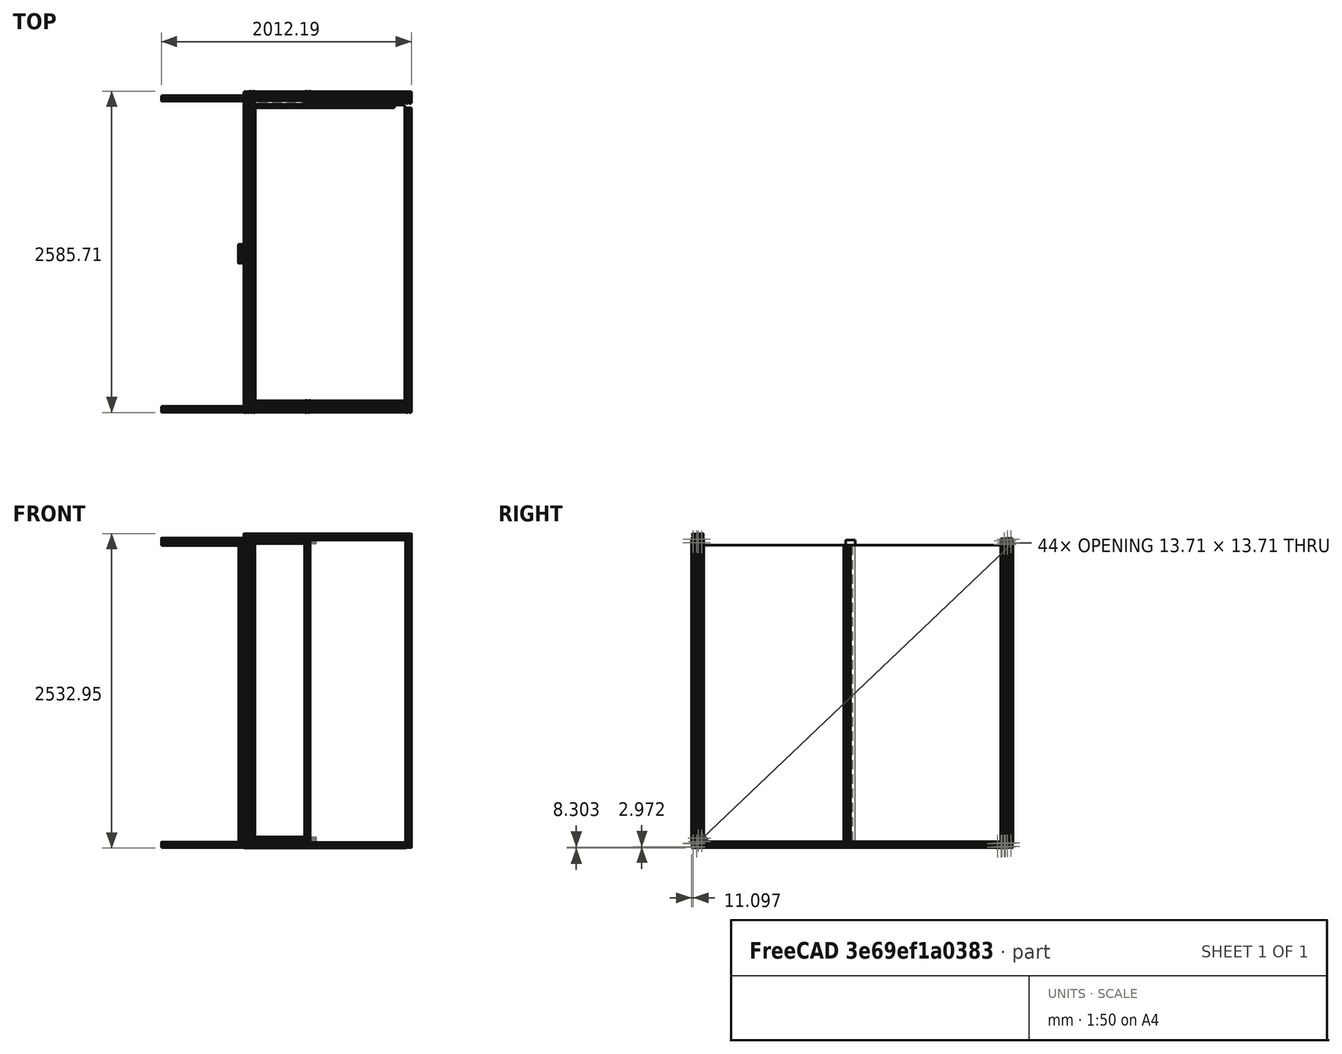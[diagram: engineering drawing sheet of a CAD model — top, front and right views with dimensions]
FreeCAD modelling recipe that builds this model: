
FCSTD DOCUMENT  (FreeCAD 0.20R)
Label: arena
License: All rights reserved
LicenseURL: http://en.wikipedia.org/wiki/All_rights_reserved
objects: PartDesign::Pad×36, PartDesign::Body×36, PartDesign::FeatureBase×28, Sketcher::SketchObject×9, Part::FeaturePython×8, App::DocumentObjectGroup×7, Part::Feature×6, TechDraw::DrawViewPart×3, TechDraw::DrawSVGTemplate×2, TechDraw::DrawPage×2, Spreadsheet::Sheet×1
note: 159 computed .brp shape members not serialized (recipe doc carries the construction recipe); baked Part::Feature solids carry a one-line shape summary decoded from their .brp

FEATURE [Part::Feature] Part__Feature  label="5537T041_T-Slotted Framing"
  shape: bbox 90 x 45 x 152.4 mm, 277 faces (baked)
FEATURE [Part::FeaturePython] Facebinder  label="double"  # WARN: FeaturePython — macro-defined, semantics opaque (R4)
  Area = 1339.39
  Extrusion = 0
  Faces = -> [Part__Feature]
  RemoveSplitter = false
  Sew = false
FEATURE [PartDesign::FeatureBase] BaseFeature
  BaseFeature = -> Facebinder
FEATURE [PartDesign::Pad] Pad
  BaseFeature = -> BaseFeature
  Direction = (0,0,1)
  Length = 2438.4
  Length2 = 10
  Profile = -> BaseFeature
  Type = 0
FEATURE [PartDesign::Body] Body  label="bottom"
  BaseFeature = -> Facebinder
  Group = -> [BaseFeature,Pad]
  Origin = -> Origin
  Placement = pos=(95.0976,0,46.5582) rot=(0,0,1;0rad)
  Tip = -> Pad
FEATURE [PartDesign::FeatureBase] BaseFeature001
  BaseFeature = -> Facebinder
FEATURE [PartDesign::Pad] Pad001
  BaseFeature = -> BaseFeature001
  Direction = (0,0,1)
  Length = 1348.13
  Length2 = 10
  Profile = -> BaseFeature001
  Type = 0
FEATURE [PartDesign::Body] Body001  label="wall"
  BaseFeature = -> Facebinder
  Group = -> [BaseFeature001,Pad001]
  Origin = -> Origin001
  Placement = pos=(-25.4,27.7368,101.6) rot=(0.57735,-0.57735,0.57735;4.18879rad)
  Tip = -> Pad001
FEATURE [Part::Feature] Part__Feature001  label="single-extrusion"
  shape: bbox 45 x 45 x 152.4 mm, 246 faces (baked)
FEATURE [Part::FeaturePython] Facebinder001  label="single001-face"  # WARN: FeaturePython — macro-defined, semantics opaque (R4)
  Area = 538.918
  Extrusion = 0
  Faces = -> [Part__Feature001]
  RemoveSplitter = false
  Sew = false
FEATURE [PartDesign::FeatureBase] BaseFeature002
  BaseFeature = -> Facebinder001
FEATURE [PartDesign::Pad] Pad002
  BaseFeature = -> BaseFeature002
  Direction = (0,0,1)
  Length = 2438.4
  Length2 = 10
  Profile = -> BaseFeature002
  Type = 0
FEATURE [PartDesign::Body] Body002  label="top001"
  BaseFeature = -> Facebinder001
  Group = -> [BaseFeature002,Pad002]
  Origin = -> Origin002
  Placement = pos=(1375.94,0,48.5394) rot=(0,0,1;0rad)
  Tip = -> Pad002
FEATURE [PartDesign::FeatureBase] BaseFeature003
  BaseFeature = -> Facebinder001
FEATURE [PartDesign::Pad] Pad003
  BaseFeature = -> BaseFeature003
  Direction = (0,0,1)
  Length = 2438.4
  Length2 = 10
  Profile = -> BaseFeature003
  Type = 0
FEATURE [PartDesign::Body] Body003  label="center"
  BaseFeature = -> Facebinder001
  Group = -> [BaseFeature003,Pad003]
  Origin = -> Origin003
  Placement = pos=(561.213,0,50.8) rot=(0,0,1;0rad)
  Tip = -> Pad003
FEATURE [PartDesign::FeatureBase] BaseFeature004
  BaseFeature = -> Facebinder001
FEATURE [PartDesign::Pad] Pad004
  BaseFeature = -> BaseFeature004
  Direction = (0,0,1)
  Length = 2438.4
  Length2 = 10
  Profile = -> BaseFeature004
  Type = 0
FEATURE [PartDesign::Body] Body004  label="bottom-window"
  BaseFeature = -> Facebinder001
  Group = -> [BaseFeature004,Pad004]
  Origin = -> Origin004
  Placement = pos=(114.3,51.511,48.539) rot=(0,0,1;0rad)
  Tip = -> Pad004
FEATURE [Part::Feature] Part__Feature002  label="single003"
  shape: bbox 45 x 45 x 152.4 mm, 246 faces (baked)
FEATURE [Part::FeaturePython] Facebinder002  label="single002"  # WARN: FeaturePython — macro-defined, semantics opaque (R4)
  Area = 538.918
  Extrusion = 0
  Faces = -> [Part__Feature002]
  RemoveSplitter = false
  Sew = false
FEATURE [PartDesign::FeatureBase] BaseFeature005
  BaseFeature = -> Facebinder002
FEATURE [PartDesign::Pad] Pad005
  BaseFeature = -> BaseFeature005
  Direction = (0,0,1)
  Length = 2438.4
  Length2 = 10
  Profile = -> BaseFeature005
  Type = 0
FEATURE [PartDesign::Body] Body005  label="top-window001"
  BaseFeature = -> Facebinder002
  Group = -> [BaseFeature005,Pad005]
  Origin = -> Origin005
  Placement = pos=(564.185,51.511,48.539) rot=(0,0,1;0rad)
  Tip = -> Pad005
FEATURE [PartDesign::FeatureBase] BaseFeature006
  BaseFeature = -> Facebinder002
FEATURE [PartDesign::Pad] Pad006
  BaseFeature = -> BaseFeature006
  Direction = (0,0,1)
  Length = 490.322
  Length2 = 10
  Profile = -> BaseFeature006
  Type = 0
  expr: Length = <<Spreadsheet>>.window_height
FEATURE [PartDesign::Body] Body006  label="window-wall"
  BaseFeature = -> Facebinder002
  Group = -> [BaseFeature006,Pad006]
  Origin = -> Origin006
  Placement = pos=(14.859,45.5676,103.022) rot=(0,1,0;1.5708rad)
  Tip = -> Pad006
FEATURE [Sketcher::SketchObject] Sketch
  FullyConstrained = false
  MapMode = 5
  Placement = pos=(0,0,0) rot=(1,0,0;1.5708rad)
  Support = -> [XZ_Plane008]
  sketch-geometry (4):
    g0: LineSegment StartX=932.741 StartY=2717.77 StartZ=0 EndX=1745.54 EndY=2717.77 EndZ=0
    g1: LineSegment StartX=1745.54 StartY=2717.77 StartZ=0 EndX=1745.54 EndY=279.367 EndZ=0
    g2: LineSegment StartX=1745.54 StartY=279.367 StartZ=0 EndX=932.741 EndY=279.367 EndZ=0
    g3: LineSegment StartX=932.741 StartY=279.367 StartZ=0 EndX=932.741 EndY=2717.77 EndZ=0
  constraints (10):
    c: Coincident(g0,g1)
    c: Coincident(g1,g2)
    c: Coincident(g2,g3)
    c: Coincident(g3,g0)
    c: Horizontal(g0)
    c: Horizontal(g2)
    c: Vertical(g1)
    c: Vertical(g3)
    c: DistanceY(g1,g1) = 2438.4
    c: DistanceX(g0,g0) = 812.8
FEATURE [PartDesign::Pad] Pad008
  Direction = (0,-1,2e-16)
  Length = 9.525
  Length2 = 10
  Placement = pos=(0,0,0) rot=(1,0,0;1.5708rad)
  Profile = -> Sketch
  ReferenceAxis = -> Sketch [N_Axis]
  Type = 0
FEATURE [PartDesign::Body] Body008  label="upper polycarb"
  Group = -> [Sketch,Pad008]
  Origin = -> Origin008
  Placement = pos=(-383.362,0,-162.458) rot=(0,0,1;0rad)
  Tip = -> Pad008
FEATURE [Sketcher::SketchObject] Sketch001
  FullyConstrained = false
  MapMode = 5
  Placement = pos=(0,0,0) rot=(1,0,0;1.5708rad)
  Support = -> [XZ_Plane008]
  sketch-geometry (4):
    g0: LineSegment StartX=527.842 StartY=2715.74 StartZ=0 EndX=934.242 EndY=2715.74 EndZ=0
    g1: LineSegment StartX=934.242 StartY=2715.74 StartZ=0 EndX=934.242 EndY=277.345 EndZ=0
    g2: LineSegment StartX=934.242 StartY=277.345 StartZ=0 EndX=527.842 EndY=277.345 EndZ=0
    g3: LineSegment StartX=527.842 StartY=277.345 StartZ=0 EndX=527.842 EndY=2715.74 EndZ=0
  constraints (10):
    c: Coincident(g0,g1)
    c: Coincident(g1,g2)
    c: Coincident(g2,g3)
    c: Coincident(g3,g0)
    c: Horizontal(g0)
    c: Horizontal(g2)
    c: Vertical(g1)
    c: Vertical(g3)
    c: DistanceY(g1,g1) = 2438.4
    c: DistanceX(g0,g0) = 406.4
FEATURE [PartDesign::Pad] Pad009
  Direction = (0,-1,2e-16)
  Length = 9.525
  Length2 = 10
  Placement = pos=(0,0,0) rot=(1,0,0;1.5708rad)
  Profile = -> Sketch001
  ReferenceAxis = -> Sketch001 [N_Axis]
  Type = 0
FEATURE [PartDesign::Body] Body009  label="lower polycarb"
  Group = -> [Sketch001,Pad009]
  Origin = -> Origin009
  Placement = pos=(-389.306,54.483,-162.458) rot=(0,0,1;0rad)
  Tip = -> Pad009
FEATURE [Part::FeaturePython] Facebinder003  label="double001"  # WARN: FeaturePython — macro-defined, semantics opaque (R4)
  Area = 1339.39
  Extrusion = 0
  Faces = -> [Part__Feature]
  RemoveSplitter = false
  Sew = false
FEATURE [PartDesign::FeatureBase] BaseFeature008
  BaseFeature = -> Facebinder003
FEATURE [PartDesign::Pad] Pad010
  BaseFeature = -> BaseFeature008
  Direction = (0,0,1)
  Length = 2438.4
  Length2 = 10
  Profile = -> BaseFeature008
  Type = 0
FEATURE [PartDesign::Body] Body010  label="bottom001"
  BaseFeature = -> Facebinder003
  Group = -> [BaseFeature008,Pad010]
  Origin = -> Origin010
  Placement = pos=(96.0882,40.6146,103.022) rot=(1,0,0;1.5708rad)
  Tip = -> Pad010
FEATURE [Part::FeaturePython] Facebinder004  label="single001-face001"  # WARN: FeaturePython — macro-defined, semantics opaque (R4)
  Area = 538.918
  Extrusion = 0
  Faces = -> [Part__Feature001]
  RemoveSplitter = false
  Sew = false
FEATURE [PartDesign::FeatureBase] BaseFeature009
  BaseFeature = -> Facebinder004
FEATURE [PartDesign::Pad] Pad011
  BaseFeature = -> BaseFeature009
  Direction = (0,0,1)
  Length = 2387.6
  Length2 = 10
  Profile = -> BaseFeature009
  Type = 0
  expr: Length = <<Spreadsheet>>.horizontal_length
FEATURE [PartDesign::Body] Body011  label="top"
  BaseFeature = -> Facebinder004
  Group = -> [BaseFeature009,Pad011]
  Origin = -> Origin011
  Placement = pos=(1375.94,17.8308,101.041) rot=(1,0,0;1.5708rad)
  Tip = -> Pad011
FEATURE [PartDesign::FeatureBase] BaseFeature010
  BaseFeature = -> Facebinder004
FEATURE [PartDesign::Pad] Pad012
  BaseFeature = -> BaseFeature010
  Direction = (0,0,1)
  Length = 1213.36
  Length2 = 10
  Profile = -> BaseFeature010
  Type = 0
  expr: Length = <<Spreadsheet>>.side_length
FEATURE [PartDesign::Body] Body012  label="side"
  BaseFeature = -> Facebinder004
  Group = -> [BaseFeature010,Pad012]
  Origin = -> Origin012
  Placement = pos=(-25.7556,-35.6616,98.0694) rot=(0,1,0;1.5708rad)
  Tip = -> Pad012
FEATURE [Sketcher::SketchObject] Sketch002
  FullyConstrained = false
  MapMode = 5
  Support = -> [XY_Plane013]
  sketch-geometry (4):
    g0: LineSegment StartX=127.47 StartY=-36.9995 StartZ=0 EndX=1346.67 EndY=-36.9995 EndZ=0
    g1: LineSegment StartX=1346.67 StartY=-36.9995 StartZ=0 EndX=1346.67 EndY=-2475.4 EndZ=0
    g2: LineSegment StartX=1346.67 StartY=-2475.4 StartZ=0 EndX=127.47 EndY=-2475.4 EndZ=0
    g3: LineSegment StartX=127.47 StartY=-2475.4 StartZ=0 EndX=127.47 EndY=-36.9995 EndZ=0
  constraints (10):
    c: Coincident(g0,g1)
    c: Coincident(g1,g2)
    c: Coincident(g2,g3)
    c: Coincident(g3,g0)
    c: Horizontal(g0)
    c: Horizontal(g2)
    c: Vertical(g1)
    c: Vertical(g3)
    c: DistanceX(g0,g0) = 1219.2
    c: DistanceY(g1,g1) = 2438.4
FEATURE [PartDesign::Pad] Pad013
  Direction = (0,0,1)
  Length = 9.525
  Length2 = 10
  Profile = -> Sketch002
  ReferenceAxis = -> Sketch002 [N_Axis]
  Type = 0
FEATURE [PartDesign::Body] Body013  label="side-polycarb"
  Group = -> [Sketch002,Pad013]
  Origin = -> Origin013
  Placement = pos=(0,0,93.1164) rot=(0,0,1;0rad)
  Tip = -> Pad013
FEATURE [PartDesign::FeatureBase] BaseFeature011
  BaseFeature = -> Facebinder004
FEATURE [PartDesign::Pad] Pad014
  BaseFeature = -> BaseFeature011
  Direction = (0,0,1)
  Length = 1303.02
  Length2 = 10
  Profile = -> BaseFeature011
  Type = 0
FEATURE [PartDesign::Body] Body014  label="side001"
  BaseFeature = -> Facebinder004
  Group = -> [BaseFeature011,Pad014]
  Origin = -> Origin014
  Placement = pos=(-25.7556,-2486.41,98.0694) rot=(0,1,0;1.5708rad)
  Tip = -> Pad014
FEATURE [App::DocumentObjectGroup] Group001  label="static-side"
  Group = -> [Facebinder003,Body010,Body011,Body012,Body013,Body014]
FEATURE [Spreadsheet::Sheet] Spreadsheet
  cells = C1=length; D1=length (mm); E1=quantity; F1=price per; G1=price; A2=static-sides; A3=bottom; B3=4590x96; C3=94; D3(horizontal_length)==C3 * 25.4; E3=2; F3=140; G3==E3 * F3; A4=top; B4=4545x96; C4=94; D4==C4 * 25.4; E4=2; F4=44; G4==E4 * F4; A5=sides; B5=4545x48; C5=47.77; D5(side_length)==C5 * 25.4; E5=4; F5=23; G5==E5 * F5; A6=polycarb; C6==C5 + 2 * 0.5; A8=window-sides; A9=bottom; B9=4590x96; C9=94; D9==C9 * 25.4; E9=2; F9=140; G9==E9 * F9; A10=top; B10=4545x96; C10=94; D10==C10 * 25.4; E10=2; F10=44; G10==E10 * F10; A11=sides; B11=4545x48; C11=53.08; D11==C11 * 25.4; E11=4; F11=23; G11==E11 * F11; A12=top/bot; B12=4545x96; C12=94; D12==C12 * 25.4; E12=4; F12=44; G12==E12 * F12; A13=sides; B13=4545x18; C13==15.76 + 2 * 1.772; D13(window_height)==C13 * 25.4; E13=4; F13=10; G13==E13 * F13; A15=roof; A16=crossbar; B16=4545x96; C16=94; D16==C16 * 25.4; E16=1; F16=44; G16==E16 * F16; A17=feet; B17=4545x32; C17=26; D17(foot_length)==C17 * 25.4; E17=5; A18=floor-brace; B18=4545; C18==C3; A19=floor-brace-support; B19=4545; C19=6; F19=total; G19==sum(G3:G16)
FEATURE [PartDesign::FeatureBase] BaseFeature012
  BaseFeature = -> Facebinder002
FEATURE [PartDesign::Pad] Pad015
  BaseFeature = -> BaseFeature012
  Direction = (0,0,1)
  Length = 490.322
  Length2 = 10
  Profile = -> BaseFeature012
  Type = 0
  expr: Length = <<Spreadsheet>>.window_height
FEATURE [PartDesign::Body] Body015  label="window-wall001"
  BaseFeature = -> Facebinder002
  Group = -> [BaseFeature012,Pad015]
  Origin = -> Origin015
  Placement = pos=(64.389,45.5676,2548.81) rot=(0,1,0;1.5708rad)
  Tip = -> Pad015
FEATURE [PartDesign::FeatureBase] BaseFeature013
  BaseFeature = -> Facebinder004
FEATURE [PartDesign::Pad] Pad016
  BaseFeature = -> BaseFeature013
  Direction = (0,0,1)
  Length = 2387.6
  Length2 = 10
  Profile = -> BaseFeature013
  Type = 0
  expr: Length = <<Spreadsheet>>.horizontal_length
FEATURE [PartDesign::Body] Body016  label="crossbar"
  BaseFeature = -> Facebinder004
  Group = -> [BaseFeature013,Pad016]
  Origin = -> Origin016
  Placement = pos=(1375.94,-1264.01,44.577) rot=(0,0,1;0rad)
  Tip = -> Pad016
FEATURE [App::DocumentObjectGroup] Group002  label="roof"
  Group = -> [Body016]
FEATURE [PartDesign::FeatureBase] BaseFeature014
  BaseFeature = -> Facebinder004
FEATURE [PartDesign::Pad] Pad017
  BaseFeature = -> BaseFeature014
  Direction = (0,0,1)
  Length = 660.4
  Length2 = 10
  Profile = -> BaseFeature014
  Type = 0
  expr: Length = <<Spreadsheet>>.foot_length
FEATURE [PartDesign::Body] Body017  label="foot"
  BaseFeature = -> Facebinder004
  Group = -> [BaseFeature014,Pad017]
  Origin = -> Origin017
  Placement = pos=(-689.458,17.8308,101.041) rot=(0.57735,0.57735,0.57735;2.0944rad)
  Tip = -> Pad017
FEATURE [Sketcher::SketchObject] Sketch003  label="people"
  FullyConstrained = false
  MapMode = 5
  Placement = pos=(0,0,0) rot=(1,0,0;1.5708rad)
  Support = -> [XZ_Plane013]
  sketch-geometry (8):
    g0: LineSegment StartX=-565.128 StartY=2175.86 StartZ=0 EndX=1212.87 EndY=2175.86 EndZ=0
    g1: LineSegment StartX=1212.87 StartY=2175.86 StartZ=0 EndX=1212.87 EndY=1762.45 EndZ=0
    g2: LineSegment StartX=1212.87 StartY=1762.45 StartZ=0 EndX=-565.128 EndY=1762.45 EndZ=0
    g3: LineSegment StartX=-565.128 StartY=1762.45 StartZ=0 EndX=-565.128 EndY=2175.86 EndZ=0
    g4: LineSegment StartX=-565.128 StartY=669.762 StartZ=0 EndX=654.072 EndY=669.762 EndZ=0
    g5: LineSegment StartX=654.072 StartY=669.762 StartZ=0 EndX=654.072 EndY=256.353 EndZ=0
    g6: LineSegment StartX=654.072 StartY=256.353 StartZ=0 EndX=-565.128 EndY=256.353 EndZ=0
    g7: LineSegment StartX=-565.128 StartY=256.353 StartZ=0 EndX=-565.128 EndY=669.762 EndZ=0
  constraints (20):
    c: Coincident(g0,g1)
    c: Coincident(g1,g2)
    c: Coincident(g2,g3)
    c: Coincident(g3,g0)
    c: Horizontal(g0)
    c: Horizontal(g2)
    c: Vertical(g1)
    c: Vertical(g3)
    c: Coincident(g4,g5)
    c: Coincident(g5,g6)
    c: Coincident(g6,g7)
    c: Coincident(g7,g4)
    c: Horizontal(g4)
    c: Horizontal(g6)
    c: Vertical(g5)
    c: Vertical(g7)
    c: DistanceX(g0,g0) = 1778
    c: DistanceX(g4,g4) = 1219.2
    c: Vertical(g2,g4)
    c: Equal(g3,g7)
FEATURE [PartDesign::FeatureBase] BaseFeature015
  BaseFeature = -> Facebinder004
FEATURE [PartDesign::Pad] Pad018
  BaseFeature = -> BaseFeature015
  Direction = (0,0,1)
  Length = 660.4
  Length2 = 10
  Profile = -> BaseFeature015
  Type = 0
  expr: Length = <<Spreadsheet>>.foot_length
FEATURE [PartDesign::Body] Body018  label="foot001"
  BaseFeature = -> Facebinder004
  Group = -> [BaseFeature015,Pad018]
  Origin = -> Origin018
  Placement = pos=(-689.458,17.8308,2535.94) rot=(0.57735,0.57735,0.57735;2.0944rad)
  Tip = -> Pad018
FEATURE [PartDesign::FeatureBase] BaseFeature016
  BaseFeature = -> Facebinder004
FEATURE [PartDesign::Pad] Pad019
  BaseFeature = -> BaseFeature016
  Direction = (0,0,1)
  Length = 660.4
  Length2 = 10
  Profile = -> BaseFeature016
  Type = 0
  expr: Length = <<Spreadsheet>>.foot_length
FEATURE [PartDesign::Body] Body019  label="foot002"
  BaseFeature = -> Facebinder004
  Group = -> [BaseFeature016,Pad019]
  Origin = -> Origin019
  Placement = pos=(-689.458,-2486.41,101.041) rot=(0.57735,0.57735,0.57735;2.0944rad)
  Tip = -> Pad019
FEATURE [PartDesign::FeatureBase] BaseFeature017
  BaseFeature = -> Facebinder004
FEATURE [PartDesign::Pad] Pad020
  BaseFeature = -> BaseFeature017
  Direction = (0,0,1)
  Length = 660.4
  Length2 = 10
  Profile = -> BaseFeature017
  Type = 0
  expr: Length = <<Spreadsheet>>.foot_length
FEATURE [PartDesign::Body] Body020  label="foot003"
  BaseFeature = -> Facebinder004
  Group = -> [BaseFeature017,Pad020]
  Origin = -> Origin020
  Placement = pos=(-689.458,-2485.42,2549.8) rot=(0.57735,0.57735,0.57735;2.0944rad)
  Tip = -> Pad020
FEATURE [App::DocumentObjectGroup] Group003  label="feet"
  Group = -> [Body017,Body018,Body019,Body020]
FEATURE [Part::Feature] Part__Feature003  label="5537T041_T-Slotted Framing001"
  shape: bbox 90 x 45 x 152.4 mm, 277 faces (baked)
FEATURE [Part::FeaturePython] Facebinder005  label="double002"  # WARN: FeaturePython — macro-defined, semantics opaque (R4)
  Area = 1339.39
  Extrusion = 0
  Faces = -> [Part__Feature003]
  RemoveSplitter = false
  Sew = false
FEATURE [PartDesign::FeatureBase] BaseFeature018
  BaseFeature = -> Facebinder005
FEATURE [PartDesign::FeatureBase] BaseFeature019
  BaseFeature = -> Facebinder005
FEATURE [PartDesign::Pad] Pad021
  BaseFeature = -> BaseFeature018
  Direction = (0,0,1)
  Length = 2438.4
  Length2 = 10
  Profile = -> BaseFeature018
  Type = 0
FEATURE [PartDesign::Body] Body021  label="bottom002"
  BaseFeature = -> Facebinder005
  Group = -> [BaseFeature018,Pad021]
  Origin = -> Origin021
  Placement = pos=(95.098,-2489.2,46.558) rot=(0,0,1;0rad)
  Tip = -> Pad021
FEATURE [PartDesign::Pad] Pad022
  BaseFeature = -> BaseFeature019
  Direction = (0,0,1)
  Length = 1348.13
  Length2 = 10
  Profile = -> BaseFeature019
  Type = 0
FEATURE [PartDesign::Body] Body022  label="wall001"
  BaseFeature = -> Facebinder005
  Group = -> [BaseFeature019,Pad022]
  Origin = -> Origin022
  Placement = pos=(-25.4,-2461.46,2586.02) rot=(0.57735,-0.57735,0.57735;4.18879rad)
  Tip = -> Pad022
FEATURE [Part::Feature] Part__Feature004  label="single-extrusion001"
  shape: bbox 45 x 45 x 152.4 mm, 246 faces (baked)
FEATURE [Part::FeaturePython] Facebinder006  label="single001-face002"  # WARN: FeaturePython — macro-defined, semantics opaque (R4)
  Area = 538.918
  Extrusion = 0
  Faces = -> [Part__Feature004]
  RemoveSplitter = false
  Sew = false
FEATURE [PartDesign::FeatureBase] BaseFeature020
  BaseFeature = -> Facebinder006
FEATURE [PartDesign::FeatureBase] BaseFeature021
  BaseFeature = -> Facebinder006
FEATURE [PartDesign::FeatureBase] BaseFeature022
  BaseFeature = -> Facebinder006
FEATURE [PartDesign::Pad] Pad023
  BaseFeature = -> BaseFeature020
  Direction = (0,0,1)
  Length = 2438.4
  Length2 = 10
  Profile = -> BaseFeature020
  Type = 0
FEATURE [PartDesign::Body] Body023  label="top002"
  BaseFeature = -> Facebinder006
  Group = -> [BaseFeature020,Pad023]
  Origin = -> Origin023
  Placement = pos=(1375.94,-2489.2,48.539) rot=(0,0,1;0rad)
  Tip = -> Pad023
FEATURE [PartDesign::Pad] Pad024
  BaseFeature = -> BaseFeature021
  Direction = (0,0,1)
  Length = 2438.4
  Length2 = 10
  Profile = -> BaseFeature021
  Type = 0
FEATURE [PartDesign::Body] Body024  label="center001"
  BaseFeature = -> Facebinder006
  Group = -> [BaseFeature021,Pad024]
  Origin = -> Origin024
  Placement = pos=(561.213,-2489.2,50.8) rot=(0,0,1;0rad)
  Tip = -> Pad024
FEATURE [PartDesign::Pad] Pad025
  BaseFeature = -> BaseFeature022
  Direction = (0,0,1)
  Length = 2438.4
  Length2 = 10
  Profile = -> BaseFeature022
  Type = 0
FEATURE [PartDesign::Body] Body025  label="bottom-window001"
  BaseFeature = -> Facebinder006
  Group = -> [BaseFeature022,Pad025]
  Origin = -> Origin025
  Placement = pos=(114.3,-2437.69,48.539) rot=(0,0,1;0rad)
  Tip = -> Pad025
FEATURE [Part::Feature] Part__Feature005  label="single005"
  shape: bbox 45 x 45 x 152.4 mm, 246 faces (baked)
FEATURE [Part::FeaturePython] Facebinder007  label="single004"  # WARN: FeaturePython — macro-defined, semantics opaque (R4)
  Area = 538.918
  Extrusion = 0
  Faces = -> [Part__Feature005]
  RemoveSplitter = false
  Sew = false
FEATURE [PartDesign::FeatureBase] BaseFeature023
  BaseFeature = -> Facebinder007
FEATURE [PartDesign::FeatureBase] BaseFeature024
  BaseFeature = -> Facebinder007
FEATURE [PartDesign::FeatureBase] BaseFeature025
  BaseFeature = -> Facebinder007
FEATURE [PartDesign::Pad] Pad026
  BaseFeature = -> BaseFeature023
  Direction = (0,0,1)
  Length = 2438.4
  Length2 = 10
  Profile = -> BaseFeature023
  Type = 0
FEATURE [PartDesign::Body] Body026  label="top-window002"
  BaseFeature = -> Facebinder007
  Group = -> [BaseFeature023,Pad026]
  Origin = -> Origin026
  Placement = pos=(564.185,-2437.69,48.539) rot=(0,0,1;0rad)
  Tip = -> Pad026
FEATURE [PartDesign::Pad] Pad027
  BaseFeature = -> BaseFeature024
  Direction = (0,0,1)
  Length = 490.322
  Length2 = 10
  Profile = -> BaseFeature024
  Type = 0
  expr: Length = <<Spreadsheet>>.window_height
FEATURE [PartDesign::Body] Body027  label="window-wall002"
  BaseFeature = -> Facebinder007
  Group = -> [BaseFeature024,Pad027]
  Origin = -> Origin027
  Placement = pos=(64.389,-2443.63,142.646) rot=(0,1,0;1.5708rad)
  Tip = -> Pad027
FEATURE [PartDesign::Pad] Pad030
  BaseFeature = -> BaseFeature025
  Direction = (0,0,1)
  Length = 490.322
  Length2 = 10
  Profile = -> BaseFeature025
  Type = 0
  expr: Length = <<Spreadsheet>>.window_height
FEATURE [PartDesign::Body] Body030  label="window-wall003"
  BaseFeature = -> Facebinder007
  Group = -> [BaseFeature025,Pad030]
  Origin = -> Origin030
  Placement = pos=(64.389,-2443.63,2548.81) rot=(0,1,0;1.5708rad)
  Tip = -> Pad030
FEATURE [Sketcher::SketchObject] Sketch004
  FullyConstrained = false
  MapMode = 5
  Placement = pos=(0,0,0) rot=(1,0,0;1.5708rad)
  Support = -> [XZ_Plane028]
  sketch-geometry (4):
    g0: LineSegment StartX=932.741 StartY=2717.77 StartZ=0 EndX=1745.54 EndY=2717.77 EndZ=0
    g1: LineSegment StartX=1745.54 StartY=2717.77 StartZ=0 EndX=1745.54 EndY=279.367 EndZ=0
    g2: LineSegment StartX=1745.54 StartY=279.367 StartZ=0 EndX=932.741 EndY=279.367 EndZ=0
    g3: LineSegment StartX=932.741 StartY=279.367 StartZ=0 EndX=932.741 EndY=2717.77 EndZ=0
  constraints (10):
    c: Coincident(g0,g1)
    c: Coincident(g1,g2)
    c: Coincident(g2,g3)
    c: Coincident(g3,g0)
    c: Horizontal(g0)
    c: Horizontal(g2)
    c: Vertical(g1)
    c: Vertical(g3)
    c: DistanceY(g1,g1) = 2438.4
    c: DistanceX(g0,g0) = 812.8
FEATURE [PartDesign::Pad] Pad028
  Direction = (0,-1,2e-16)
  Length = 9.525
  Length2 = 10
  Placement = pos=(0,0,0) rot=(1,0,0;1.5708rad)
  Profile = -> Sketch004
  ReferenceAxis = -> Sketch004 [N_Axis]
  Type = 0
FEATURE [PartDesign::Body] Body028  label="upper polycarb001"
  Group = -> [Sketch004,Pad028]
  Origin = -> Origin028
  Placement = pos=(-383.362,-2489.2,-162.458) rot=(0,0,1;0rad)
  Tip = -> Pad028
FEATURE [Sketcher::SketchObject] Sketch005
  FullyConstrained = false
  MapMode = 5
  Placement = pos=(0,0,0) rot=(1,0,0;1.5708rad)
  Support = -> [XZ_Plane028]
  sketch-geometry (4):
    g0: LineSegment StartX=527.842 StartY=2715.74 StartZ=0 EndX=934.242 EndY=2715.74 EndZ=0
    g1: LineSegment StartX=934.242 StartY=2715.74 StartZ=0 EndX=934.242 EndY=277.345 EndZ=0
    g2: LineSegment StartX=934.242 StartY=277.345 StartZ=0 EndX=527.842 EndY=277.345 EndZ=0
    g3: LineSegment StartX=527.842 StartY=277.345 StartZ=0 EndX=527.842 EndY=2715.74 EndZ=0
  constraints (10):
    c: Coincident(g0,g1)
    c: Coincident(g1,g2)
    c: Coincident(g2,g3)
    c: Coincident(g3,g0)
    c: Horizontal(g0)
    c: Horizontal(g2)
    c: Vertical(g1)
    c: Vertical(g3)
    c: DistanceY(g1,g1) = 2438.4
    c: DistanceX(g0,g0) = 406.4
FEATURE [PartDesign::Pad] Pad029
  Direction = (0,-1,2e-16)
  Length = 9.525
  Length2 = 10
  Placement = pos=(0,0,0) rot=(1,0,0;1.5708rad)
  Profile = -> Sketch005
  ReferenceAxis = -> Sketch005 [N_Axis]
  Type = 0
FEATURE [PartDesign::Body] Body029  label="lower polycarb001"
  Group = -> [Sketch005,Pad029]
  Origin = -> Origin029
  Placement = pos=(-389.306,-2434.72,-162.458) rot=(0,0,1;0rad)
  Tip = -> Pad029
FEATURE [App::DocumentObjectGroup] Group004  label="window-side001"
  Group = -> [Part__Feature003,Facebinder005,Body021,Body022,Body023,Part__Feature004,Facebinder006,Body024,Body025,Body026,Facebinder007,Part__Feature005,Body027,Body028,Body029,Body030]
FEATURE [Sketcher::SketchObject] Sketch006
  FullyConstrained = false
  MapMode = 5
  Placement = pos=(0,0,0) rot=(0.57735,0.57735,0.57735;2.0944rad)
  Support = -> [YZ_Plane031]
  sketch-geometry (4):
    g0: LineSegment StartX=-2452 StartY=2515.94 StartZ=0 EndX=-1232.8 EndY=2515.94 EndZ=0
    g1: LineSegment StartX=-1232.8 StartY=2515.94 StartZ=0 EndX=-1232.8 EndY=128.339 EndZ=0
    g2: LineSegment StartX=-1232.8 StartY=128.339 StartZ=0 EndX=-2452 EndY=128.339 EndZ=0
    g3: LineSegment StartX=-2452 StartY=128.339 StartZ=0 EndX=-2452 EndY=2515.94 EndZ=0
  constraints (10):
    c: Coincident(g0,g1)
    c: Coincident(g1,g2)
    c: Coincident(g2,g3)
    c: Coincident(g3,g0)
    c: Horizontal(g0)
    c: Horizontal(g2)
    c: Vertical(g1)
    c: Vertical(g3)
    c: DistanceX(g0,g0) = 1219.2
    c: DistanceY(g1,g1) = 2387.6
FEATURE [PartDesign::Pad] Pad031
  Direction = (1,-2e-16,3e-16)
  Length = 19.05
  Length2 = 10
  Placement = pos=(0,0,0) rot=(0.57735,0.57735,0.57735;2.0944rad)
  Profile = -> Sketch006
  ReferenceAxis = -> Sketch006 [N_Axis]
  Type = 0
FEATURE [PartDesign::Body] Body031  label="plywood"
  Group = -> [Sketch006,Pad031]
  Origin = -> Origin031
  Placement = pos=(49.53,0,0) rot=(0,0,1;0rad)
  Tip = -> Pad031
FEATURE [Sketcher::SketchObject] Sketch007
  FullyConstrained = false
  MapMode = 5
  Placement = pos=(0,0,0) rot=(0.57735,0.57735,0.57735;2.0944rad)
  Support = -> [YZ_Plane032]
  sketch-geometry (4):
    g0: LineSegment StartX=-2452 StartY=2515.94 StartZ=0 EndX=-1232.8 EndY=2515.94 EndZ=0
    g1: LineSegment StartX=-1232.8 StartY=2515.94 StartZ=0 EndX=-1232.8 EndY=128.339 EndZ=0
    g2: LineSegment StartX=-1232.8 StartY=128.339 StartZ=0 EndX=-2452 EndY=128.339 EndZ=0
    g3: LineSegment StartX=-2452 StartY=128.339 StartZ=0 EndX=-2452 EndY=2515.94 EndZ=0
  constraints (10):
    c: Coincident(g0,g1)
    c: Coincident(g1,g2)
    c: Coincident(g2,g3)
    c: Coincident(g3,g0)
    c: Horizontal(g0)
    c: Horizontal(g2)
    c: Vertical(g1)
    c: Vertical(g3)
    c: DistanceX(g0,g0) = 1219.2
    c: DistanceY(g1,g1) = 2387.6
FEATURE [PartDesign::Pad] Pad032
  Direction = (1,-2e-16,3e-16)
  Length = 19.05
  Length2 = 10
  Placement = pos=(0,0,0) rot=(0.57735,0.57735,0.57735;2.0944rad)
  Profile = -> Sketch007
  ReferenceAxis = -> Sketch007 [N_Axis]
  Type = 0
FEATURE [PartDesign::Body] Body032  label="plywood001"
  Group = -> [Sketch007,Pad032]
  Origin = -> Origin032
  Placement = pos=(52.5018,1218.44,0) rot=(0,0,1;0rad)
  Tip = -> Pad032
FEATURE [PartDesign::FeatureBase] BaseFeature026
  BaseFeature = -> Facebinder002
FEATURE [PartDesign::Pad] Pad033
  BaseFeature = -> BaseFeature026
  Direction = (0,0,1)
  Length = 1213.36
  Length2 = 10
  Profile = -> BaseFeature026
  Type = 0
  expr: Length = <<Spreadsheet>>.side_length
FEATURE [PartDesign::Body] Body033  label="side002"
  BaseFeature = -> Facebinder002
  Group = -> [BaseFeature026,Pad033]
  Origin = -> Origin033
  Placement = pos=(-25.7556,0,100.051) rot=(0,1,0;1.5708rad)
  Tip = -> Pad033
FEATURE [App::DocumentObjectGroup] Group  label="window-side"
  Group = -> [Part__Feature,Facebinder,Body,Body001,Body002,Part__Feature001,Facebinder001,Body003,Body004,Body005,Facebinder002,Part__Feature002,Body006,Body008,Body009,Body015,Body033]
FEATURE [PartDesign::FeatureBase] BaseFeature027
  BaseFeature = -> Facebinder001
FEATURE [PartDesign::Pad] Pad034
  BaseFeature = -> BaseFeature027
  Direction = (0,0,1)
  Length = 2387.6
  Length2 = 10
  Profile = -> BaseFeature027
  Type = 0
  expr: Length = <<Spreadsheet>>.horizontal_length
FEATURE [PartDesign::Body] Body034  label="floor-brace"
  BaseFeature = -> Facebinder001
  Group = -> [BaseFeature027,Pad034]
  Origin = -> Origin034
  Placement = pos=(32.6898,-1240.23,2586.46) rot=(1,0,0;3.14159rad)
  Tip = -> Pad034
FEATURE [Sketcher::SketchObject] Sketch008
  FullyConstrained = false
  MapMode = 5
  Support = -> [XY_Plane035]
  sketch-geometry (4):
    g0: LineSegment StartX=-217.749 StartY=107.245 StartZ=0 EndX=-141.549 EndY=107.245 EndZ=0
    g1: LineSegment StartX=-141.549 StartY=107.245 StartZ=0 EndX=-141.549 EndY=102.483 EndZ=0
    g2: LineSegment StartX=-141.549 StartY=102.483 StartZ=0 EndX=-217.749 EndY=102.483 EndZ=0
    g3: LineSegment StartX=-217.749 StartY=102.483 StartZ=0 EndX=-217.749 EndY=107.245 EndZ=0
  constraints (10):
    c: Coincident(g0,g1)
    c: Coincident(g1,g2)
    c: Coincident(g2,g3)
    c: Coincident(g3,g0)
    c: Horizontal(g0)
    c: Horizontal(g2)
    c: Vertical(g1)
    c: Vertical(g3)
    c: DistanceY(g3,g3) = 4.7625
    c: DistanceX(g2,g2) = 76.2
FEATURE [PartDesign::Pad] Pad035
  Direction = (0,0,1)
  Length = 2477.52
  Length2 = 10
  Profile = -> Sketch008
  ReferenceAxis = -> Sketch008 [N_Axis]
  Type = 0
  expr: Length = 94in + 2 * 1.77in
FEATURE [PartDesign::Body] Body035  label="floor-brace001"
  Group = -> [Sketch008,Pad035]
  Origin = -> Origin035
  Placement = pos=(151.562,-1053.01,80.2386) rot=(0,0,1;1.5708rad)
  Tip = -> Pad035
FEATURE [PartDesign::FeatureBase] BaseFeature028
  BaseFeature = -> Facebinder001
FEATURE [PartDesign::Pad] Pad036
  BaseFeature = -> BaseFeature028
  Direction = (0,0,1)
  Length = 152.4
  Length2 = 10
  Profile = -> BaseFeature028
  Type = 0
FEATURE [PartDesign::Body] Body036  label="floor-support"
  BaseFeature = -> Facebinder001
  Group = -> [BaseFeature028,Pad036]
  Origin = -> Origin036
  Placement = pos=(27.7368,-1080.74,104.013) rot=(1,0,0;1.5708rad)
  Tip = -> Pad036
FEATURE [App::DocumentObjectGroup] Group005  label="floor"
  Group = -> [Body031,Body032,Body034,Body035,Body036]
FEATURE [TechDraw::DrawSVGTemplate] Template
  EditableTexts = Designed_by_Name=Adam Spontarelli; Drawing_number=Drawing number; FC-Date=Date; FC-SC=Scale; FC-Title=Title; Subtitle=Subtitle
  Height = 215.9
  Orientation = 1
  Width = 279.4
FEATURE [TechDraw::DrawViewPart] View
  CoarseView = false
  Direction = (0.356,-0.743,-0.566)
  Focus = 100
  HardHidden = true
  IsoCount = 0
  IsoHidden = false
  IsoVisible = false
  LockPosition = false
  Perspective = false
  Rotation = 0
  ScaleType = 1
  SeamHidden = false
  SeamVisible = true
  SmoothHidden = false
  SmoothVisible = true
  Source = -> [Template]
  X = 139.7
  XDirection = (0.003,0.607,-0.795)
  Y = 107.95
FEATURE [TechDraw::DrawSVGTemplate] Template001
  EditableTexts = Designed_by_Name=Designed by Name; Drawing_number=Drawing number; FC-Date=Date; FC-SC=Scale; FC-SH=Sheet; FC-Title=Title; Subtitle=Subtitle; Weight=Weight
  Height = 210
  Orientation = 1
  Width = 297
FEATURE [TechDraw::DrawViewPart] View002
  CoarseView = false
  Direction = (0,0,-1)
  Focus = 100
  HardHidden = true
  IsoCount = 0
  IsoHidden = false
  IsoVisible = false
  LockPosition = false
  Perspective = false
  Rotation = 0
  Scale = 0.1
  ScaleType = 1
  SeamHidden = false
  SeamVisible = true
  SmoothHidden = false
  SmoothVisible = true
  Source = -> [Body010,Body011,Body012,Body013,Body014]
  X = 145.817
  XDirection = (0,1,0)
  Y = 128.809
FEATURE [TechDraw::DrawPage] Page001
  KeepUpdated = true
  NextBalloonIndex = 1
  ProjectionType = 0
  Scale = 0.5
  Template = -> Template001
  Views = -> [View002]
FEATURE [App::DocumentObjectGroup] Group006  label="drawings"
  Group = -> [Page]
FEATURE [TechDraw::DrawPage] Page
  KeepUpdated = true
  NextBalloonIndex = 1
  ProjectionType = 0
  Template = -> Template
  Views = -> [View,View001]
FEATURE [TechDraw::DrawViewPart] View001
  CoarseView = false
  Direction = (0.356,-0.743,-0.566)
  Focus = 100
  HardHidden = true
  IsoCount = 0
  IsoHidden = false
  IsoVisible = false
  LockPosition = false
  Perspective = false
  Rotation = 0
  Scale = 0.05
  ScaleType = 1
  SeamHidden = false
  SeamVisible = true
  SmoothHidden = false
  SmoothVisible = true
  Source = -> [Group,Group001,Facebinder004,Spreadsheet,Group002,Group003,Sketch003,Group004,Group005,Group006]
  X = 122.351
  XDirection = (0.003,0.607,-0.795)
  Y = 114.697
